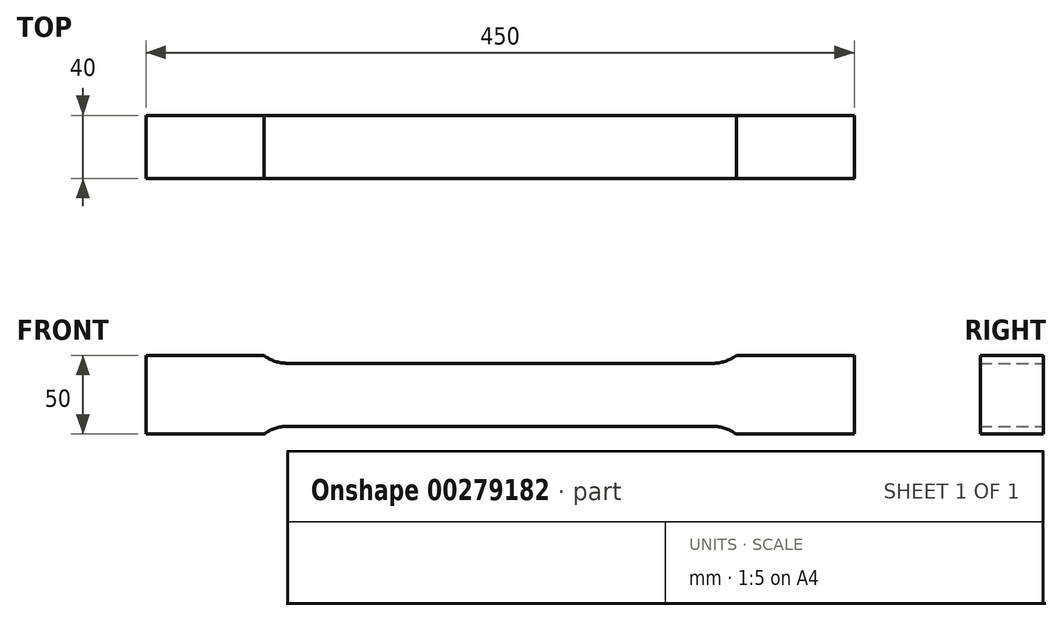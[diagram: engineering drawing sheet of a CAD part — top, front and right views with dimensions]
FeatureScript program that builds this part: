
annotation { "Feature Type Name" : "Feature", "Feature Type Description" : "" }
export const myFeature = defineFeature(function(context is Context, id is Id, definition is map)
    precondition{}
    {
        {
            var Q0;
            Q0=qCreatedBy(makeId("Front.planeOp"),FACE);
            var sketch = newSketch(context, id + "F0", { "sketchPlane" : qUnion([Q0])});
            skLineSegment(sketch, "E0", {"start": v(0, 20) * mm, "end": v(135, 20) * mm});
            skArc(sketch, "E1", {"start": v(135, 20) * mm, "mid": v(142.9, 21.28) * mm, "end": v(150, 25) * mm});
            skLineSegment(sketch, "E2", {"start": v(150, 25) * mm, "end": v(225, 25) * mm});
            skLineSegment(sketch, "E3", {"start": v(225, 25) * mm, "end": v(225, 0) * mm});
            skLineSegment(sketch, "E4.MirrorCS", {"start": v(0, -20) * mm, "end": v(135, -20) * mm});
            skLineSegment(sketch, "E5.MirrorCS", {"start": v(225, -25) * mm, "end": v(225, 0) * mm});
            skLineSegment(sketch, "E6.MirrorCS", {"start": v(150, -25) * mm, "end": v(225, -25) * mm});
            skArc(sketch, "E7.MirrorCS", {"start": v(135, -20) * mm, "mid": v(142.9, -21.28) * mm, "end": v(150, -25) * mm});
            skArc(sketch, "E8.MirrorCS", {"start": v(-135, -20) * mm, "mid": v(-142.9, -21.28) * mm, "end": v(-150, -25) * mm});
            skLineSegment(sketch, "E9.MirrorCS", {"start": v(-150, -25) * mm, "end": v(-225, -25) * mm});
            skArc(sketch, "E10.MirrorCS", {"start": v(-135, 20) * mm, "mid": v(-142.9, 21.28) * mm, "end": v(-150, 25) * mm});
            skLineSegment(sketch, "E11.MirrorCS", {"start": v(-150, 25) * mm, "end": v(-225, 25) * mm});
            skLineSegment(sketch, "E12.MirrorCS", {"start": v(-225, -25) * mm, "end": v(-225, 0) * mm});
            skLineSegment(sketch, "E13.MirrorCS", {"start": v(0, -20) * mm, "end": v(-135, -20) * mm});
            skLineSegment(sketch, "E14.MirrorCS", {"start": v(-225, 25) * mm, "end": v(-225, 0) * mm});
            skLineSegment(sketch, "E15.MirrorCS", {"start": v(0, 20) * mm, "end": v(-135, 20) * mm});
            skSolve(sketch);
        }
        {
            var Q0;
            Q0=makeQuery(id+"F0.imprint","IMPRINT",FACE,{"disambiguationData":[TD([[makeQuery(id+"F0.imprint","IMPRINT",EDGE,{"derivedFrom":sQuery(id+"F0.wireOp",EDGE,"E0")}),-1.0]])]});
            extrude(context, id + "F1", {"entities" : qUnion([Q0]), "endBound" : BoundingType.SYMMETRIC, "depth" : 40 * mm});
        }
    });
